# Revit family: Urinal-Wall_Mount-KOHLER-Dexter-K-5016LM
name_source: partatom
category: Plumbing Fixtures
revit_build: Autodesk Revit 2017 (Build: 20160225_1515(x64)
units: mm (PartAtom-declared; Revit-internal decimal feet)

## family parameters
Cut with Voids When Loaded = No
Host = Face
OmniClass Number = 23.31.21.00
OmniClass Title = Urinals
Part Type = Normal
Room Calculation Point = No
Round Connector Dimension = Use Diameter
Shared = No

## types (4) — shared parameters
ADA Compliant = No
Assembly Code = D2010200
CW Connection = Yes
Cold Water Inlet = Cold Water Inlet
Date Modified = 03/24/2021
Default Elevation = 0"
Description = Urinal Dexter
Flow Rate = 0 GPM
Flush Rate- GPF = 1.0 GPF
Flush Rate- LPF = 3.8 LPF
HW Connection = No
Height = 20 3/8"
Hot Water Inlet = Hot Water Inlet
Length = 14 1/2"
Manufacturer = KOHLER Co.
Master Format 2014 = 22 41 13.16
Master Format 2014 Name = Residential Urinals
Material = Vitreous China
Pressure = 0.00 psi
Product Name = Dexter
URL = https://la.kohler.com
Vent Connection = No
Waste Connection = Yes
Waste Water Outlet = Waste Water Outlet
WaterSense Certified = No
Width = 13 1/2"

## per-type parameters (varying)
| type | Finish | Model | Type |
| 0-White | Kohler-Vitreous_China-0-White | K-5016LM-ET-0 | 1 |
| 7-Black Black | Kohler-Vitreous_China-7-Black_Black | K-5016LM-ET-7 | 2 |
| 47-Almond | Kohler-Vitreous_China-47-Almond | K-5016LM-ET-47 | 3 |
| 96-Biscuit | Kohler-Vitreous_China-96-Biscuit | K-5016LM-ET-96 | 4 |

## geometry (parser evidence)
native form markers: Sweep x3
no freeform markers — native parametric forms only
